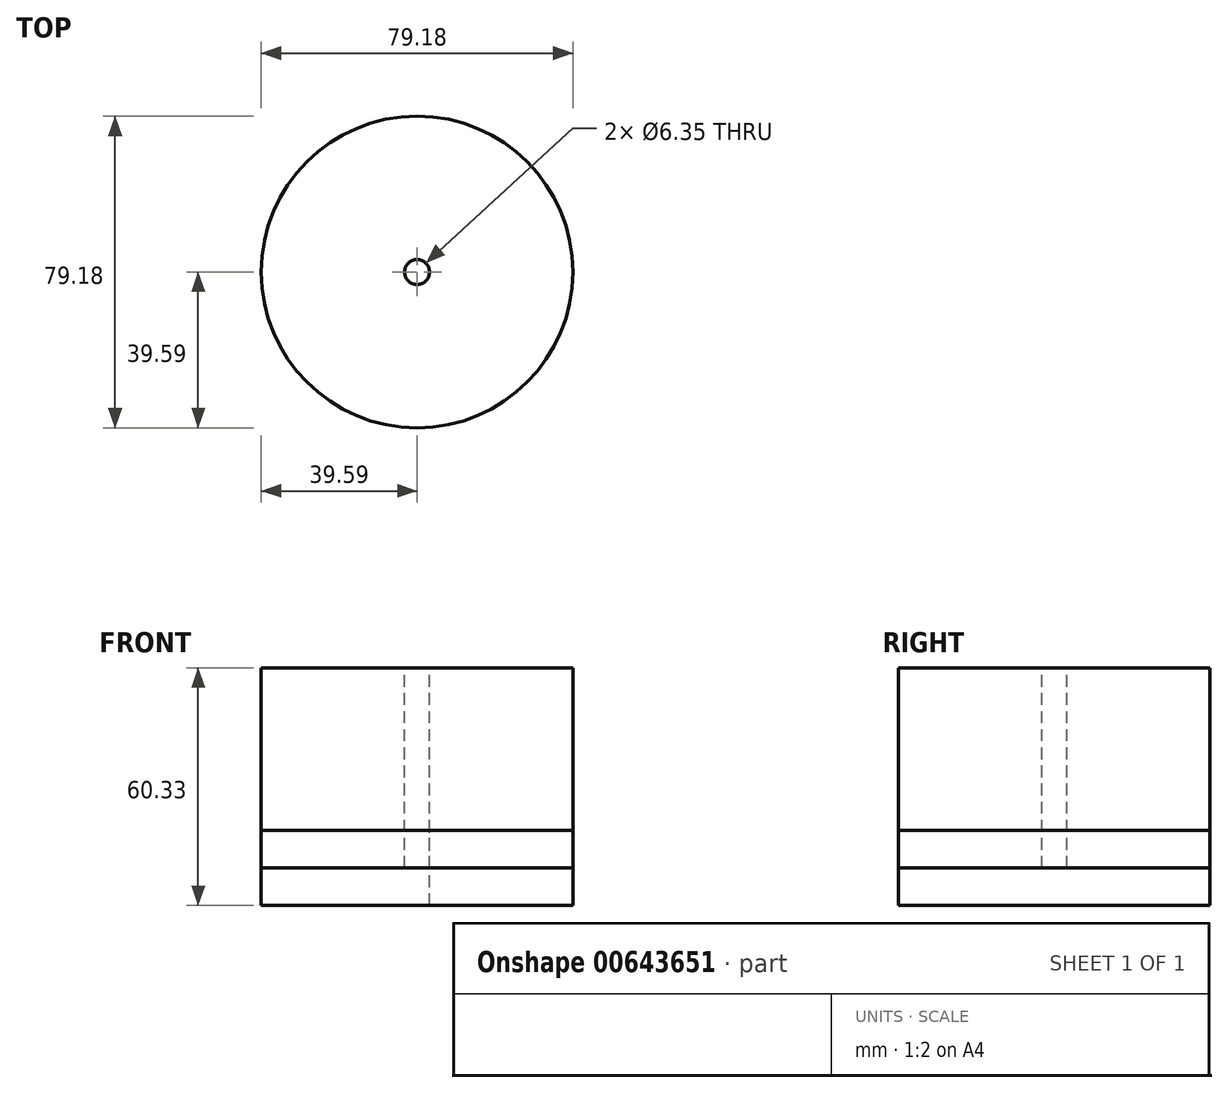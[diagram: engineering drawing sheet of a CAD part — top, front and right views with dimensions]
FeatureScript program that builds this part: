
annotation { "Feature Type Name" : "Feature", "Feature Type Description" : "" }
export const myFeature = defineFeature(function(context is Context, id is Id, definition is map)
    precondition{}
    {
        {
            var Q0;
            Q0=qCreatedBy(makeId("Top.planeOp"),FACE);
            var sketch = newSketch(context, id + "F0", { "sketchPlane" : qUnion([Q0])});
            skCircle(sketch, "E0", {"center": v(0, 0) * mm, "radius": 39.6 * mm});
            skSolve(sketch);
        }
        {
            var Q0;
            Q0 = qSketchRegion(id + "F4KpMswZuqZbG3u_1", true);
            var Q1;
            Q1 = qSketchRegion(id + "FP84oXrXUb1QaaY_0", true);
            var Q2;
            Q2 = qSketchRegion(id + "F0", true);
            extrude(context, id + "F1", {"entities" : qUnion([Q0, Q1, Q2]), "endBound" : BoundingType.SYMMETRIC, "depth" : 19.05 * mm, "offsetDistance" : 25.4 * mm});
        }
        {
            var Q0;
            Q0=makeQuery(id+"F0.imprint","IMPRINT",FACE,{"disambiguationData":[TD([[makeQuery(id+"F0.imprint","IMPRINT",EDGE,{"derivedFrom":sQuery(id+"F0.wireOp",EDGE,"E0")}),1.0]])]});
            var Q1;
            Q1 = qSketchRegion(id + "F4KpMswZuqZbG3u_1", true);
            extrude(context, id + "F2", {"entities" : qUnion([Q0, Q1]), "depth" : 50.8 * mm, "offsetDistance" : 25.4 * mm});
        }
        {
            var Q0;
            Q0=makeQuery(id+"F2.opExtrude","CAP_FACE",FACE,{"disambiguationData":[OSD([sQuery(id+"F0.wireOp",EDGE,"E0")])],"isStart":false});
            var sketch = newSketch(context, id + "F3", { "sketchPlane" : qUnion([Q0])});
            skCircle(sketch, "E1", {"center": v(0, 0) * mm, "radius": 31.2 * mm});
            skSolve(sketch);
        }
        {
            var Q0;
            Q0=sQuery(id+"F3.wireOp",VERTEX,"E1.center");
            var Q1;
            Q1=makeQuery(id+"F1.opExtrude","SWEPT_BODY",BODY,{"disambiguationData":[OSD([sQuery(id+"F0.wireOp",EDGE,"E0")])]});
            var Q2;
            Q2=makeQuery(id+"F2.opExtrude","SWEPT_BODY",BODY,{"disambiguationData":[OSD([sQuery(id+"F0.wireOp",EDGE,"E0")])]});
            hole(context, id + "F4", {"style" : HoleStyle.SIMPLE, "endStyle" : HoleEndStyle.THROUGH, "holeDiameter" : 6.35 * mm, "majorDiameter" : 6.35 * mm, "isTappedThrough" : true, "tappedDepth" : 12.7 * mm, "tapClearance" : 3, "locations" : qUnion([Q0]), "scope" : qUnion([Q1, Q2])});
        }
    });
